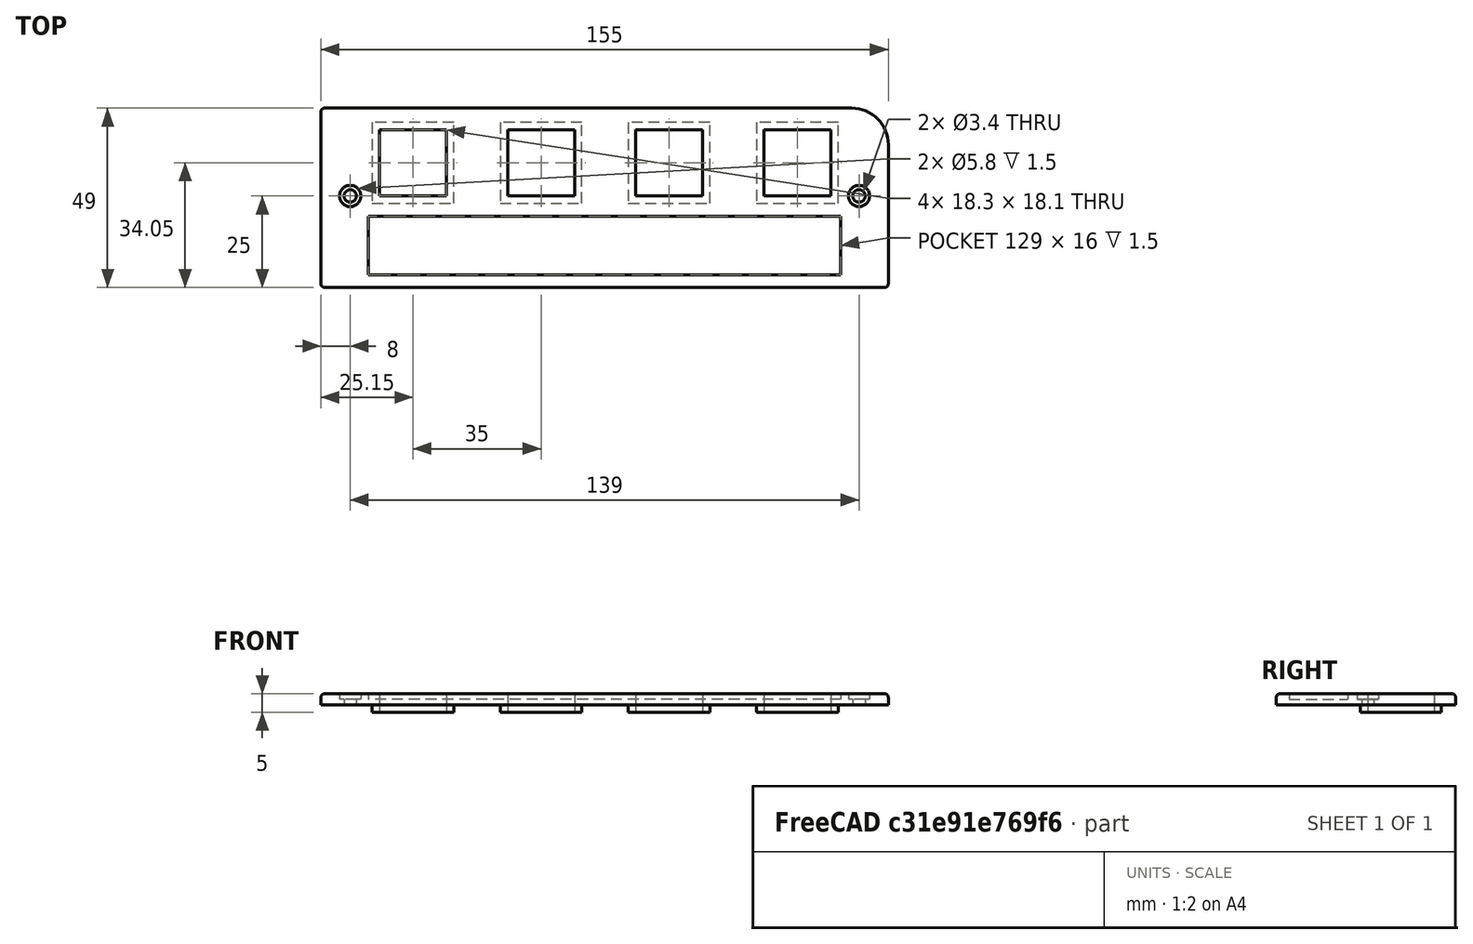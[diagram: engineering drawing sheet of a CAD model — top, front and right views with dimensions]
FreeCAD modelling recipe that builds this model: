
FCSTD DOCUMENT  (FreeCAD 0.20R29603 (Git))
Label: EnjoliveurBoutonsDroiteAvecFixation
License: All rights reserved
LicenseURL: http://en.wikipedia.org/wiki/All_rights_reserved
objects: TechDraw::DrawViewDimension×24, Sketcher::SketchObject×5, TechDraw::DrawViewPart×4, PartDesign::Fillet×3, TechDraw::DrawViewAnnotation×3, PartDesign::Pad×2, PartDesign::Pocket×2, PartDesign::LinearPattern×2, TechDraw::DrawSVGTemplate×2, TechDraw::DrawPage×2, PartDesign::Hole×1, PartDesign::Body×1, TechDraw::DrawViewDetail×1
note: 24 computed .brp shape members not serialized (recipe doc carries the construction recipe); baked Part::Feature solids carry a one-line shape summary decoded from their .brp

FEATURE [Sketcher::SketchObject] Sketch
  FullyConstrained = true
  MapMode = 5
  Support = -> [XY_Plane]
  sketch-geometry (5):
    g0: LineSegment StartX=145 StartY=49 StartZ=0 EndX=0 EndY=49 EndZ=0
    g1: LineSegment StartX=0 StartY=49 StartZ=0 EndX=0 EndY=0 EndZ=0
    g2: LineSegment StartX=0 StartY=0 StartZ=0 EndX=155 EndY=0 EndZ=0
    g3: LineSegment StartX=155 StartY=0 StartZ=0 EndX=155 EndY=39 EndZ=0
    g4: ArcOfCircle CenterX=145 CenterY=39 CenterZ=0 NormalX=0 NormalY=0 NormalZ=1 AngleXU=0 Radius=10 StartAngle=1.24e-14 EndAngle=1.5708
  constraints (13):
    c: Coincident(g0,g1)
    c: Horizontal(g0)
    c: Vertical(g1)
    c: DistanceY(g1,g1) = 49
    c: Coincident(g1,g2)
    c: Horizontal(g2)
    c: Coincident(g2,g3)
    c: Vertical(g3)
    c: DistanceX(g2,g2) = 155
    c: Coincident(g1,g-1)
    c: Radius(g4) = 10
    c: Tangent(g4,g0) = -1.5708
    c: Tangent(g4,g3) = -1.5708
FEATURE [PartDesign::Pad] Pad  label="Main body"
  Direction = (0,0,1)
  Length = 3
  Length2 = 100
  Profile = -> Sketch
  Type = 0
FEATURE [Sketcher::SketchObject] Sketch001  label="Trou carre bouton sketch"
  ExternalGeometry = -> [Pad]
  FullyConstrained = true
  MapMode = 5
  Placement = pos=(0,0,3) rot=(0,0,1;0rad)
  Support = -> [Pad]
  sketch-geometry (4):
    g0: LineSegment StartX=16 StartY=43.1 StartZ=0 EndX=34.3 EndY=43.1 EndZ=0
    g1: LineSegment StartX=34.3 StartY=43.1 StartZ=0 EndX=34.3 EndY=25 EndZ=0
    g2: LineSegment StartX=34.3 StartY=25 StartZ=0 EndX=16 EndY=25 EndZ=0
    g3: LineSegment StartX=16 StartY=25 StartZ=0 EndX=16 EndY=43.1 EndZ=0
  constraints (12):
    c: Coincident(g0,g1)
    c: Coincident(g1,g2)
    c: Coincident(g2,g3)
    c: Coincident(g3,g0)
    c: Horizontal(g0)
    c: Horizontal(g2)
    c: Vertical(g1)
    c: Vertical(g3)
    c: DistanceY(g1,g1) = 18.1
    c: DistanceX(g0,g0) = 18.3
    c: DistanceY(g0,g-3) = 5.9
    c: DistanceX(g2) = 16
FEATURE [PartDesign::Pocket] Pocket  label="Trou carre bouton"
  BaseFeature = -> Pad
  Direction = (0,0,-1)
  Length = 5
  Length2 = 5
  Profile = -> Sketch001
  ReferenceAxis = -> Sketch001 [N_Axis]
  Type = 1
FEATURE [PartDesign::LinearPattern] LinearPattern  label="Trous carres boutons"
  BaseFeature = -> Pocket
  Direction = -> Sketch001 [H_Axis]
  Length = 105
  Occurrences = 4
  Originals = -> [Pocket]
FEATURE [Sketcher::SketchObject] Sketch002  label="Labels boutons sketch"
  FullyConstrained = true
  MapMode = 5
  Placement = pos=(0,0,3) rot=(0,0,1;0rad)
  Support = -> [LinearPattern]
  sketch-geometry (4):
    g0: LineSegment StartX=13 StartY=19.5 StartZ=0 EndX=142 EndY=19.5 EndZ=0
    g1: LineSegment StartX=142 StartY=19.5 StartZ=0 EndX=142 EndY=3.5 EndZ=0
    g2: LineSegment StartX=142 StartY=3.5 StartZ=0 EndX=13 EndY=3.5 EndZ=0
    g3: LineSegment StartX=13 StartY=3.5 StartZ=0 EndX=13 EndY=19.5 EndZ=0
  constraints (12):
    c: Coincident(g0,g1)
    c: Coincident(g1,g2)
    c: Coincident(g2,g3)
    c: Coincident(g3,g0)
    c: Horizontal(g0)
    c: Horizontal(g2)
    c: Vertical(g1)
    c: Vertical(g3)
    c: DistanceX(g0,g0) = 129
    c: DistanceY(g1,g1) = 16
    c: DistanceY(g2) = 3.5
    c: DistanceX(g0) = 13
FEATURE [PartDesign::Pocket] Pocket001  label="Labels boutons"
  BaseFeature = -> LinearPattern
  Direction = (0,0,-1)
  Length = 1.5
  Length2 = 5
  Profile = -> Sketch002
  ReferenceAxis = -> Sketch002 [N_Axis]
  Type = 0
FEATURE [Sketcher::SketchObject] Sketch003  label="Trous fixation sketch"
  ExternalGeometry = -> [Pocket001]
  FullyConstrained = true
  MapMode = 5
  Placement = pos=(0,0,3) rot=(0,0,1;0rad)
  Support = -> [Pocket001]
  sketch-geometry (2):
    g0: Circle CenterX=8 CenterY=25 CenterZ=0 NormalX=0 NormalY=0 NormalZ=1 AngleXU=0 Radius=1.5
    g1: Circle CenterX=147 CenterY=25 CenterZ=0 NormalX=0 NormalY=0 NormalZ=1 AngleXU=0 Radius=1.5
  constraints (7):
    c: Horizontal(g0,g1)
    c: Diameter(g0) = 3
    c: Diameter(g1) = 3
    c: DistanceY(g0) = 25
    c: DistanceX(g1,g-3) = 8
    c: DistanceX(g0) = 8
    c: DistanceX(g0,g1) = 139
FEATURE [PartDesign::Hole] Hole  label="Trous fixation"
  BaseFeature = -> Pocket001
  CustomThreadClearance = 0
  Depth = 328.429
  DepthType = 1
  Diameter = 3.4
  DrillForDepth = false
  DrillPoint = 1
  DrillPointAngle = 118
  HoleCutCountersinkAngle = 90
  HoleCutCustomValues = false
  HoleCutDepth = 1.5
  HoleCutDiameter = 5.8
  HoleCutType = 1
  ModelThread = false
  Profile = -> Sketch003
  Tapered = false
  TaperedAngle = 90
  ThreadClass = 0
  ThreadDepth = 328.429
  ThreadDepthType = 0
  ThreadDirection = 0
  ThreadFit = 0
  ThreadSize = 9
  ThreadType = 1
  Threaded = false
  UseCustomThreadClearance = false
FEATURE [TechDraw::DrawSVGTemplate] Template
  EditableTexts = Designed_by_Name=Designed by Name; Drawing_number=Drawing number; FC-Date=Date; FC-SC=Scale; FC-SH=Sheet; FC-Title=Enjoliveur boutons droite; Subtitle=Vues de face et de dos; Weight=Weight
  Height = 210
  Orientation = 1
  Width = 297
FEATURE [Sketcher::SketchObject] Sketch004  label="Carre centrage bouton sketch"
  ExternalGeometry = -> [Hole]
  FullyConstrained = true
  MapMode = 5
  Placement = pos=(0,0,0) rot=(1,0,0;3.14159rad)
  Support = -> [Hole]
  sketch-geometry (8):
    g0: LineSegment StartX=16 StartY=-25 StartZ=0 EndX=34.3 EndY=-25 EndZ=0
    g1: LineSegment StartX=34.3 StartY=-25 StartZ=0 EndX=34.3 EndY=-43.1 EndZ=0
    g2: LineSegment StartX=34.3 StartY=-43.1 StartZ=0 EndX=16 EndY=-43.1 EndZ=0
    g3: LineSegment StartX=16 StartY=-43.1 StartZ=0 EndX=16 EndY=-25 EndZ=0
    g4: LineSegment StartX=14 StartY=-23 StartZ=0 EndX=36.3 EndY=-23 EndZ=0
    g5: LineSegment StartX=36.3 StartY=-23 StartZ=0 EndX=36.3 EndY=-45.1 EndZ=0
    g6: LineSegment StartX=36.3 StartY=-45.1 StartZ=0 EndX=14 EndY=-45.1 EndZ=0
    g7: LineSegment StartX=14 StartY=-45.1 StartZ=0 EndX=14 EndY=-23 EndZ=0
  constraints (22):
    c: Coincident(g0,g1)
    c: Coincident(g1,g2)
    c: Coincident(g2,g3)
    c: Coincident(g3,g0)
    c: Horizontal(g0)
    c: Horizontal(g2)
    c: Vertical(g1)
    c: Vertical(g3)
    c: Coincident(g4,g5)
    c: Coincident(g5,g6)
    c: Coincident(g6,g7)
    c: Coincident(g7,g4)
    c: Horizontal(g4)
    c: Horizontal(g6)
    c: Vertical(g5)
    c: Vertical(g7)
    c: Coincident(g0,g-3)
    c: Coincident(g-4,g1)
    c: DistanceX(g0,g4) = 2
    c: DistanceY(g0,g4) = 2
    c: DistanceX(g6,g2) = 2
    c: DistanceY(g5,g1) = 2
FEATURE [PartDesign::Pad] Pad001  label="Carre centrage bouton"
  BaseFeature = -> Hole
  Direction = (0,0,-1)
  Length = 2
  Length2 = 10
  Profile = -> Sketch004
  ReferenceAxis = -> Sketch004 [N_Axis]
  Type = 0
FEATURE [PartDesign::LinearPattern] LinearPattern001
  BaseFeature = -> Pad001
  Direction = -> Sketch004 [H_Axis]
  Length = 105
  Occurrences = 4
  Originals = -> [Pad001]
FEATURE [PartDesign::Fillet] Fillet
  Base = -> LinearPattern001 [Edge4]
  BaseFeature = -> LinearPattern001
  Radius = 1
  SupportTransform = false
  UseAllEdges = false
FEATURE [PartDesign::Fillet] Fillet001
  Base = -> Fillet [Edge38]
  BaseFeature = -> Fillet
  Radius = 1
  SupportTransform = false
  UseAllEdges = false
FEATURE [PartDesign::Fillet] Fillet002
  Base = -> Fillet001 [Edge36]
  BaseFeature = -> Fillet001
  Radius = 1
  SupportTransform = false
  UseAllEdges = false
FEATURE [PartDesign::Body] Body  label="Body part1"
  Group = -> [Sketch,Pad,Sketch001,Pocket,LinearPattern,Sketch002,Pocket001,Sketch003,Hole,Sketch004,Pad001,LinearPattern001,Fillet,Fillet001,Fillet002]
  Origin = -> Origin
  Tip = -> Fillet002
FEATURE [TechDraw::DrawViewPart] View  label="Vue face"
  CoarseView = false
  Direction = (0,0,1)
  Focus = 100
  HardHidden = false
  IsoCount = 0
  IsoHidden = false
  IsoVisible = false
  LockPosition = false
  Perspective = false
  Rotation = 0
  ScaleType = 0
  SeamHidden = false
  SeamVisible = false
  SmoothHidden = false
  SmoothVisible = false
  Source = -> [Fillet002]
  X = 148.792
  XDirection = (1,0,0)
  Y = 160.125
FEATURE [TechDraw::DrawViewPart] View001  label="Vue dos"
  CoarseView = false
  Direction = (0,0,-1)
  Focus = 100
  HardHidden = false
  IsoCount = 0
  IsoHidden = false
  IsoVisible = false
  LockPosition = false
  Perspective = false
  Rotation = 0
  ScaleType = 0
  SeamHidden = false
  SeamVisible = false
  SmoothHidden = false
  SmoothVisible = false
  Source = -> [Fillet002]
  X = 148.208
  XDirection = (-1,0,0)
  Y = 90.4167
FEATURE [TechDraw::DrawViewDimension] Dimension
  AngleOverride = false
  Arbitrary = false
  ArbitraryTolerances = false
  EqualTolerance = true
  ExtensionAngle = 0
  FormatSpec = %.2w
  FormatSpecOverTolerance = %+.2w
  FormatSpecUnderTolerance = %+.2w
  Inverted = false
  LineAngle = 0
  LockPosition = false
  MeasureType = 1
  OverTolerance = 0
  References2D = -> [View]
  Rotation = 0
  ScaleType = 0
  TheoreticalExact = false
  Type = 1
  UnderTolerance = 0
  X = -1.45833
  Y = -35.3403
FEATURE [TechDraw::DrawViewDimension] Dimension001
  AngleOverride = false
  Arbitrary = false
  ArbitraryTolerances = false
  EqualTolerance = true
  ExtensionAngle = 0
  FormatSpec = %.2w
  FormatSpecOverTolerance = %+.2w
  FormatSpecUnderTolerance = %+.2w
  Inverted = false
  LineAngle = 0
  LockPosition = false
  MeasureType = 1
  OverTolerance = 0
  References2D = -> [View]
  Rotation = 0
  ScaleType = 0
  TheoreticalExact = false
  Type = 2
  UnderTolerance = 0
  X = 120.504
  Y = 2.91989
FEATURE [TechDraw::DrawViewDimension] Dimension002
  AngleOverride = false
  Arbitrary = false
  ArbitraryTolerances = false
  EqualTolerance = true
  ExtensionAngle = 0
  FormatSpec = %.2w
  FormatSpecOverTolerance = %+.2w
  FormatSpecUnderTolerance = %+.2w
  Inverted = false
  LineAngle = 0
  LockPosition = false
  MeasureType = 1
  OverTolerance = 0
  References2D = -> [View]
  Rotation = 0
  ScaleType = 0
  TheoreticalExact = false
  Type = 1
  UnderTolerance = 0
  X = -52.9577
  Y = 34.813
FEATURE [TechDraw::DrawViewDimension] Dimension003
  AngleOverride = false
  Arbitrary = false
  ArbitraryTolerances = false
  EqualTolerance = true
  ExtensionAngle = 0
  FormatSpec = %.2w
  FormatSpecOverTolerance = %+.2w
  FormatSpecUnderTolerance = %+.2w
  Inverted = false
  LineAngle = 0
  LockPosition = false
  MeasureType = 1
  OverTolerance = 0
  References2D = -> [View]
  Rotation = 0
  ScaleType = 0
  TheoreticalExact = false
  Type = 2
  UnderTolerance = 0
  X = -1.87638
  Y = 10.6832
FEATURE [TechDraw::DrawViewDimension] Dimension004
  AngleOverride = false
  Arbitrary = false
  ArbitraryTolerances = false
  EqualTolerance = true
  ExtensionAngle = 0
  FormatSpec = %.2w
  FormatSpecOverTolerance = %+.2w
  FormatSpecUnderTolerance = %+.2w
  Inverted = false
  LineAngle = 0
  LockPosition = false
  MeasureType = 1
  OverTolerance = 0
  References2D = -> [View]
  Rotation = 0
  ScaleType = 0
  TheoreticalExact = false
  Type = 1
  UnderTolerance = 0
  X = -35.0483
  Y = 34.883
FEATURE [TechDraw::DrawViewDimension] Dimension005
  AngleOverride = false
  Arbitrary = false
  ArbitraryTolerances = false
  EqualTolerance = true
  ExtensionAngle = 0
  FormatSpec = %.2w
  FormatSpecOverTolerance = %+.2w
  FormatSpecUnderTolerance = %+.2w
  Inverted = false
  LineAngle = 0
  LockPosition = false
  MeasureType = 1
  OverTolerance = 0
  References2D = -> [View]
  Rotation = 0
  ScaleType = 0
  TheoreticalExact = false
  Type = 2
  UnderTolerance = 0
  X = 85.8685
  Y = 34.5605
FEATURE [TechDraw::DrawViewDimension] Dimension006
  AngleOverride = false
  Arbitrary = false
  ArbitraryTolerances = false
  EqualTolerance = true
  ExtensionAngle = 0
  FormatSpec = %.2w
  FormatSpecOverTolerance = %+.2w
  FormatSpecUnderTolerance = %+.2w
  Inverted = false
  LineAngle = 0
  LockPosition = false
  MeasureType = 1
  OverTolerance = 0
  References2D = -> [View]
  Rotation = 0
  ScaleType = 0
  TheoreticalExact = false
  Type = 1
  UnderTolerance = 0
  X = -2.16433
  Y = -26.8288
FEATURE [TechDraw::DrawViewDimension] Dimension007
  AngleOverride = false
  Arbitrary = false
  ArbitraryTolerances = false
  EqualTolerance = true
  ExtensionAngle = 0
  FormatSpec = %.2w
  FormatSpecOverTolerance = %+.2w
  FormatSpecUnderTolerance = %+.2w
  Inverted = false
  LineAngle = 0
  LockPosition = false
  MeasureType = 1
  OverTolerance = 0
  References2D = -> [View]
  Rotation = 0
  ScaleType = 0
  TheoreticalExact = false
  Type = 2
  UnderTolerance = 0
  X = -100.101
  Y = -28.0638
FEATURE [TechDraw::DrawViewDetail] Detail  label="Detail trou fixation"
  AnchorPoint = (69.52,2.27e-14,0)
  BaseView = -> View
  CoarseView = false
  Direction = (0,0,1)
  Focus = 100
  HardHidden = false
  IsoCount = 0
  IsoHidden = false
  IsoVisible = false
  LockPosition = false
  Perspective = false
  Radius = 10
  Reference = trou fixation
  Rotation = 0
  Scale = 2
  ScaleType = 2
  SeamHidden = false
  SeamVisible = false
  SmoothHidden = false
  SmoothVisible = false
  Source = -> [Fillet002]
  X = 258.33
  XDirection = (1,0,0)
  Y = 111.656
FEATURE [TechDraw::DrawViewDimension] Dimension008
  AngleOverride = false
  Arbitrary = false
  ArbitraryTolerances = false
  EqualTolerance = true
  ExtensionAngle = 0
  FormatSpec = ⌀%.2w
  FormatSpecOverTolerance = %+.2w
  FormatSpecUnderTolerance = %+.2w
  Inverted = false
  LineAngle = 0
  LockPosition = false
  MeasureType = 1
  OverTolerance = 0
  References2D = -> [Detail]
  Rotation = 0
  ScaleType = 0
  TheoreticalExact = false
  Type = 5
  UnderTolerance = 0
  X = 20.2257
  Y = -15.3415
FEATURE [TechDraw::DrawViewDimension] Dimension009
  AngleOverride = false
  Arbitrary = false
  ArbitraryTolerances = false
  EqualTolerance = true
  ExtensionAngle = 0
  FormatSpec = ⌀%.2w
  FormatSpecOverTolerance = %+.2w
  FormatSpecUnderTolerance = %+.2w
  Inverted = false
  LineAngle = 0
  LockPosition = false
  MeasureType = 1
  OverTolerance = 0
  References2D = -> [Detail]
  Rotation = 0
  ScaleType = 0
  TheoreticalExact = false
  Type = 5
  UnderTolerance = 0
  X = 19.3034
  Y = 20.1909
FEATURE [TechDraw::DrawViewDimension] Dimension010
  AngleOverride = false
  Arbitrary = false
  ArbitraryTolerances = false
  EqualTolerance = true
  ExtensionAngle = 0
  FormatSpec = %.2w
  FormatSpecOverTolerance = %+.2w
  FormatSpecUnderTolerance = %+.2w
  Inverted = false
  LineAngle = 0
  LockPosition = false
  MeasureType = 1
  OverTolerance = 0
  References2D = -> [View001]
  Rotation = 0
  ScaleType = 0
  TheoreticalExact = false
  Type = 1
  UnderTolerance = 0
  X = -86.591
  Y = -5.97529
FEATURE [TechDraw::DrawViewDimension] Dimension011
  AngleOverride = false
  Arbitrary = false
  ArbitraryTolerances = false
  EqualTolerance = true
  ExtensionAngle = 0
  FormatSpec = %.2w
  FormatSpecOverTolerance = %+.2w
  FormatSpecUnderTolerance = %+.2w
  Inverted = false
  LineAngle = 0
  LockPosition = false
  MeasureType = 1
  OverTolerance = 0
  References2D = -> [View001]
  Rotation = 0
  ScaleType = 0
  TheoreticalExact = false
  Type = 1
  UnderTolerance = 0
  X = 60.5202
  Y = -7.72402
FEATURE [TechDraw::DrawViewDimension] Dimension012
  AngleOverride = false
  Arbitrary = false
  ArbitraryTolerances = false
  EqualTolerance = true
  ExtensionAngle = 0
  FormatSpec = %.2w
  FormatSpecOverTolerance = %+.2w
  FormatSpecUnderTolerance = %+.2w
  Inverted = false
  LineAngle = 0
  LockPosition = false
  MeasureType = 1
  OverTolerance = 0
  References2D = -> [View001]
  Rotation = 0
  ScaleType = 0
  TheoreticalExact = false
  Type = 2
  UnderTolerance = 0
  X = -99.4028
  Y = -9.76692
FEATURE [TechDraw::DrawViewDimension] Dimension013
  AngleOverride = false
  Arbitrary = false
  ArbitraryTolerances = false
  EqualTolerance = true
  ExtensionAngle = 0
  FormatSpec = %.2w
  FormatSpecOverTolerance = %+.2w
  FormatSpecUnderTolerance = %+.2w
  Inverted = false
  LineAngle = 0
  LockPosition = false
  MeasureType = 1
  OverTolerance = 0
  References2D = -> [View]
  Rotation = 0
  ScaleType = 0
  TheoreticalExact = false
  Type = 1
  UnderTolerance = 0
  X = -85.3722
  Y = -8.46548
FEATURE [TechDraw::DrawViewDimension] Dimension014
  AngleOverride = false
  Arbitrary = false
  ArbitraryTolerances = false
  EqualTolerance = true
  ExtensionAngle = 0
  FormatSpec = %.2w
  FormatSpecOverTolerance = %+.2w
  FormatSpecUnderTolerance = %+.2w
  Inverted = false
  LineAngle = 0
  LockPosition = false
  MeasureType = 1
  OverTolerance = 0
  References2D = -> [View]
  Rotation = 0
  ScaleType = 0
  TheoreticalExact = false
  Type = 2
  UnderTolerance = 0
  X = -39.5813
  Y = 10.3711
FEATURE [TechDraw::DrawViewDimension] Dimension015
  AngleOverride = false
  Arbitrary = false
  ArbitraryTolerances = false
  EqualTolerance = true
  ExtensionAngle = 0
  FormatSpec = %.2w
  FormatSpecOverTolerance = %+.2w
  FormatSpecUnderTolerance = %+.2w
  Inverted = false
  LineAngle = 0
  LockPosition = false
  MeasureType = 1
  OverTolerance = 0
  References2D = -> [View001]
  Rotation = 0
  ScaleType = 0
  TheoreticalExact = false
  Type = 1
  UnderTolerance = 0
  X = -17.9095
  Y = -7.52387
FEATURE [TechDraw::DrawViewDimension] Dimension016
  AngleOverride = false
  Arbitrary = false
  ArbitraryTolerances = false
  EqualTolerance = true
  ExtensionAngle = 0
  FormatSpec = %.2w
  FormatSpecOverTolerance = %+.2w
  FormatSpecUnderTolerance = %+.2w
  Inverted = false
  LineAngle = 0
  LockPosition = false
  MeasureType = 1
  OverTolerance = 0
  References2D = -> [View001]
  Rotation = 0
  ScaleType = 0
  TheoreticalExact = false
  Type = 2
  UnderTolerance = 0
  X = -1.57613
  Y = 11.1428
FEATURE [TechDraw::DrawSVGTemplate] Template001
  EditableTexts = Designed_by_Name=Designed by Name; Drawing_number=Drawing number; FC-Date=Date; FC-SC=Scale; FC-SH=Sheet; FC-Title=Enjoliveur boutons droite; Subtitle=Vues de profil; Weight=Weight
  Height = 210
  Orientation = 1
  Width = 297
FEATURE [TechDraw::DrawViewPart] View002
  CoarseView = true
  Direction = (0,-1,0)
  Focus = 100
  HardHidden = true
  IsoCount = 0
  IsoHidden = false
  IsoVisible = true
  LockPosition = false
  Perspective = false
  Rotation = 0
  Scale = 1.7
  ScaleType = 2
  SeamHidden = false
  SeamVisible = true
  SmoothHidden = false
  SmoothVisible = false
  Source = -> [Fillet002]
  X = 148.5
  XDirection = (1,0,0)
  Y = 183.75
FEATURE [TechDraw::DrawViewPart] View003
  CoarseView = true
  Direction = (-1,0,0)
  Focus = 100
  HardHidden = true
  IsoCount = 0
  IsoHidden = false
  IsoVisible = true
  LockPosition = false
  Perspective = false
  Rotation = 0
  Scale = 5
  ScaleType = 2
  SeamHidden = false
  SeamVisible = true
  SmoothHidden = false
  SmoothVisible = false
  Source = -> [Fillet002]
  X = 148.5
  XDirection = (0,-1,0)
  Y = 105
FEATURE [TechDraw::DrawViewAnnotation] Annotation
  Font = osifont
  LineSpace = 80
  LockPosition = false
  MaxWidth = -1
  Rotation = 0
  ScaleType = 0
  Text = Echelle 170/100
  TextSize = 5
  TextStyle = 0
  X = 263.125
  Y = 164.792
FEATURE [TechDraw::DrawViewAnnotation] Annotation001
  Font = osifont
  LineSpace = 80
  LockPosition = false
  MaxWidth = -1
  Rotation = 0
  ScaleType = 0
  Text = Echelle 500/100
  TextSize = 5
  TextStyle = 0
  X = 41.75
  Y = 76.4167
FEATURE [TechDraw::DrawViewDimension] Dimension017
  AngleOverride = false
  Arbitrary = false
  ArbitraryTolerances = false
  EqualTolerance = true
  ExtensionAngle = 0
  FormatSpec = %.2w
  FormatSpecOverTolerance = %+.2w
  FormatSpecUnderTolerance = %+.2w
  Inverted = false
  LineAngle = 0
  LockPosition = false
  MeasureType = 1
  OverTolerance = 0
  References2D = -> [View003]
  Rotation = 0
  ScaleType = 0
  TheoreticalExact = false
  Type = 1
  UnderTolerance = 0
  X = -0.140032
  Y = 46.7458
FEATURE [TechDraw::DrawViewDimension] Dimension018
  AngleOverride = false
  Arbitrary = false
  ArbitraryTolerances = false
  EqualTolerance = true
  ExtensionAngle = 0
  FormatSpec = %.2w
  FormatSpecOverTolerance = %+.2w
  FormatSpecUnderTolerance = %+.2w
  Inverted = false
  LineAngle = 0
  LockPosition = false
  MeasureType = 1
  OverTolerance = 0
  References2D = -> [View003]
  Rotation = 0
  ScaleType = 0
  TheoreticalExact = false
  Type = 1
  UnderTolerance = 0
  X = -48.0526
  Y = -15.1306
FEATURE [TechDraw::DrawViewDimension] Dimension019
  AngleOverride = false
  Arbitrary = false
  ArbitraryTolerances = false
  EqualTolerance = true
  ExtensionAngle = 0
  FormatSpec = %.2w
  FormatSpecOverTolerance = %+.2w
  FormatSpecUnderTolerance = %+.2w
  Inverted = false
  LineAngle = 0
  LockPosition = false
  MeasureType = 1
  OverTolerance = 0
  References2D = -> [View003]
  Rotation = 0
  ScaleType = 0
  TheoreticalExact = false
  Type = 1
  UnderTolerance = 0
  X = 67.1354
  Y = -16.3832
FEATURE [TechDraw::DrawViewDimension] Dimension020
  AngleOverride = false
  Arbitrary = false
  ArbitraryTolerances = false
  EqualTolerance = true
  ExtensionAngle = 0
  FormatSpec = %.2w
  FormatSpecOverTolerance = %+.2w
  FormatSpecUnderTolerance = %+.2w
  Inverted = false
  LineAngle = 0
  LockPosition = false
  MeasureType = 1
  OverTolerance = 0
  References2D = -> [View003]
  Rotation = 0
  ScaleType = 0
  TheoreticalExact = false
  Type = 2
  UnderTolerance = 0
  X = 106.518
  Y = 23.0199
FEATURE [TechDraw::DrawViewDimension] Dimension021
  AngleOverride = false
  Arbitrary = false
  ArbitraryTolerances = false
  EqualTolerance = true
  ExtensionAngle = 0
  FormatSpec = %.2w
  FormatSpecOverTolerance = %+.2w
  FormatSpecUnderTolerance = %+.2w
  Inverted = false
  LineAngle = 0
  LockPosition = false
  MeasureType = 1
  OverTolerance = 0
  References2D = -> [View003]
  Rotation = 0
  ScaleType = 0
  TheoreticalExact = false
  Type = 1
  UnderTolerance = 0
  X = 19.9654
  Y = 36.8442
FEATURE [TechDraw::DrawViewDimension] Dimension022
  AngleOverride = false
  Arbitrary = false
  ArbitraryTolerances = false
  EqualTolerance = true
  ExtensionAngle = 0
  FormatSpec = %.2w
  FormatSpecOverTolerance = %+.2w
  FormatSpecUnderTolerance = %+.2w
  Inverted = false
  LineAngle = 0
  LockPosition = false
  MeasureType = 1
  OverTolerance = 0
  References2D = -> [View003]
  Rotation = 0
  ScaleType = 0
  TheoreticalExact = false
  Type = 1
  UnderTolerance = 0
  X = 17.8665
  Y = 25.6184
FEATURE [TechDraw::DrawViewDimension] Dimension023
  AngleOverride = false
  Arbitrary = false
  ArbitraryTolerances = false
  EqualTolerance = true
  ExtensionAngle = 0
  FormatSpec = %.2w
  FormatSpecOverTolerance = %+.2w
  FormatSpecUnderTolerance = %+.2w
  Inverted = false
  LineAngle = 0
  LockPosition = false
  MeasureType = 1
  OverTolerance = 0
  References2D = -> [View003]
  Rotation = 0
  ScaleType = 0
  TheoreticalExact = false
  Type = 2
  UnderTolerance = 0
  X = 15.7754
  Y = -26.9823
FEATURE [TechDraw::DrawPage] Page001  label="Page vues profil"
  KeepUpdated = true
  NextBalloonIndex = 1
  ProjectionType = 0
  Template = -> Template001
  Views = -> [View002,View003,Annotation,Annotation001,Dimension017,Dimension018,Dimension019,Dimension020,Dimension021,Dimension022,Dimension023]
FEATURE [TechDraw::DrawViewAnnotation] Annotation002
  Font = osifont
  LineSpace = 80
  LockPosition = false
  MaxWidth = -1
  Rotation = 0
  ScaleType = 0
  Text = Vis à tôle - Tête cylindrique crucif. M 2.2 x 6.4 Zingué
  TextSize = 5
  TextStyle = 0
  X = 74.4167
  Y = 43.1667
FEATURE [TechDraw::DrawPage] Page  label="Page vues face et dos"
  KeepUpdated = true
  NextBalloonIndex = 1
  ProjectionType = 0
  Template = -> Template
  Views = -> [View,View001,Dimension,Dimension001,Dimension002,Dimension003,Dimension004,Dimension005,Dimension006,Dimension007,Detail,Dimension008,Dimension009,Dimension010,Dimension011,Dimension012,Dimension013,Dimension014,Dimension015,Dimension016,Annotation002]
